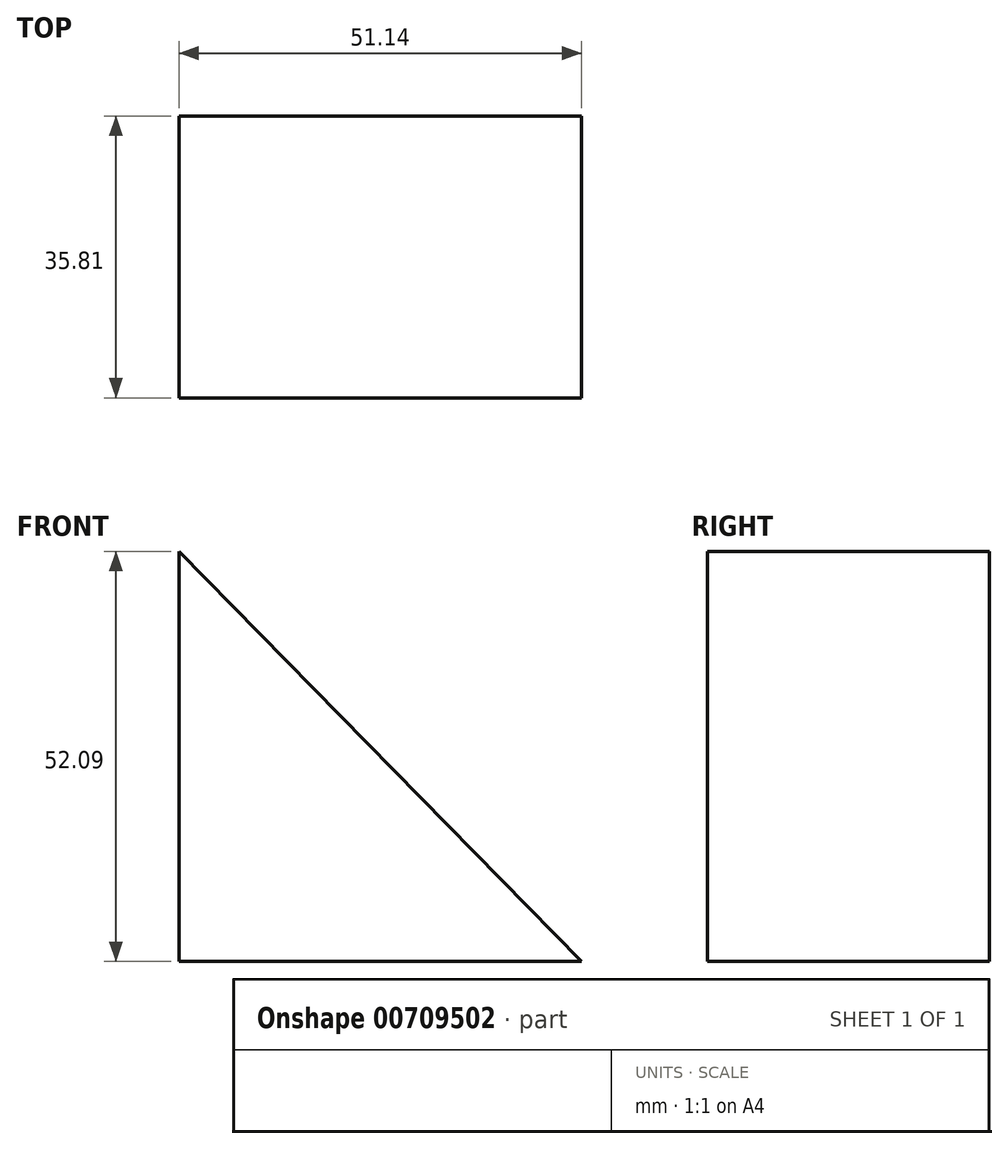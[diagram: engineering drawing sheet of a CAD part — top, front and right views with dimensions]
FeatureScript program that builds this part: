
annotation { "Feature Type Name" : "Feature", "Feature Type Description" : "" }
export const myFeature = defineFeature(function(context is Context, id is Id, definition is map)
    precondition{}
    {
        {
            var Q0;
            Q0=qCreatedBy(makeId("Front.planeOp"),FACE);
            var sketch = newSketch(context, id + "F0", { "sketchPlane" : qUnion([Q0])});
            skLineSegment(sketch, "E0", {"start": v(-54.56, 58.45) * mm, "end": v(-54.56, 6.36) * mm});
            skLineSegment(sketch, "E1", {"start": v(-54.56, 6.36) * mm, "end": v(-3.42, 6.36) * mm});
            skLineSegment(sketch, "E2", {"start": v(-3.42, 6.36) * mm, "end": v(-54.56, 58.45) * mm});
            skSolve(sketch);
        }
        {
            var Q0;
            Q0 = qSketchRegion(id + "F0", true);
            extrude(context, id + "F1", {"entities" : qUnion([Q0]), "depth" : 35.81 * mm, "offsetDistance" : 25.4 * mm});
        }
    });
